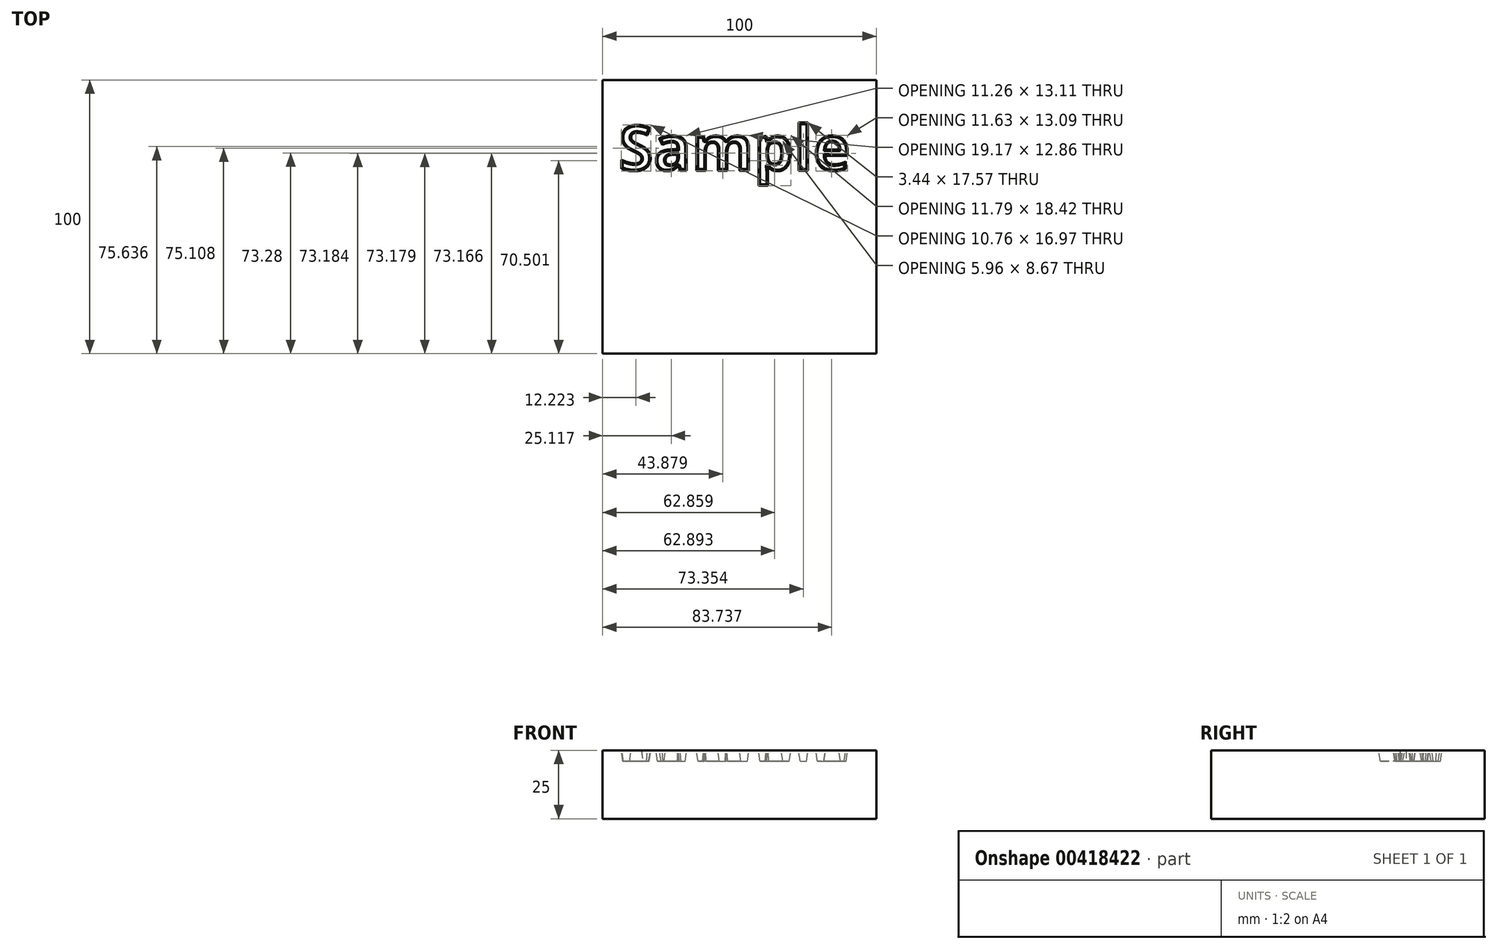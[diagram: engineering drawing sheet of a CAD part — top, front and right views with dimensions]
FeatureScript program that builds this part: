
annotation { "Feature Type Name" : "Feature", "Feature Type Description" : "" }
export const myFeature = defineFeature(function(context is Context, id is Id, definition is map)
    precondition{}
    {
        {
            var Q0;
            Q0=qCreatedBy(makeId("Top.planeOp"),FACE);
            var sketch = newSketch(context, id + "F0", { "sketchPlane" : qUnion([Q0])});
            skLineSegment(sketch, "E0.bottom", {"start": v(-41.28, 41.81) * mm, "end": v(58.72, 41.81) * mm});
            skLineSegment(sketch, "E0.top", {"start": v(-41.28, -58.19) * mm, "end": v(58.72, -58.19) * mm});
            skLineSegment(sketch, "E0.left", {"start": v(-41.28, 41.81) * mm, "end": v(-41.28, -58.19) * mm});
            skLineSegment(sketch, "E0.right", {"start": v(58.72, 41.81) * mm, "end": v(58.72, -58.19) * mm});
            skSolve(sketch);
        }
        {
            var Q0;
            Q0=makeQuery(id+"F0.imprint","IMPRINT",FACE,{"disambiguationData":[TD([[makeQuery(id+"F0.imprint","IMPRINT",EDGE,{"derivedFrom":sQuery(id+"F0.wireOp",EDGE,"E0.bottom")}),-1.0]])]});
            extrude(context, id + "F1", {"entities" : qUnion([Q0]), "depth" : 25 * mm});
        }
        {
            var Q0;
            Q0=makeQuery(id+"F1.opExtrude","CAP_FACE",FACE,{"disambiguationData":[OSD([sQuery(id+"F0.wireOp",EDGE,"E0.bottom"),sQuery(id+"F0.wireOp",EDGE,"E0.top"),sQuery(id+"F0.wireOp",EDGE,"E0.left"),sQuery(id+"F0.wireOp",EDGE,"E0.right")])],"isStart":false});
            var sketch = newSketch(context, id + "F2", { "sketchPlane" : qUnion([Q0])});
            skText(sketch, "E1", { "text": "Sample", "fontName": "OpenSans-Bold.ttf"});
            const initialGuessF2  = {"E1": [-0.0355, 0.00866, 1, 0, 0.01665]};
            skSetInitialGuess(sketch, initialGuessF2);
            skSolve(sketch);
        }
        {
            var Q0;
            Q0 = qSketchRegion(id + "F2", true);
            extrude(context, id + "F3", {"entities" : qUnion([Q0]), "operationType" : NewBodyOperationType.REMOVE, "oppositeDirection" : true, "depth" : 4 * mm, "hasDraft" : true, "draftAngle" : 8 * degree, "draftPullDirection" : true});
        }
    });
